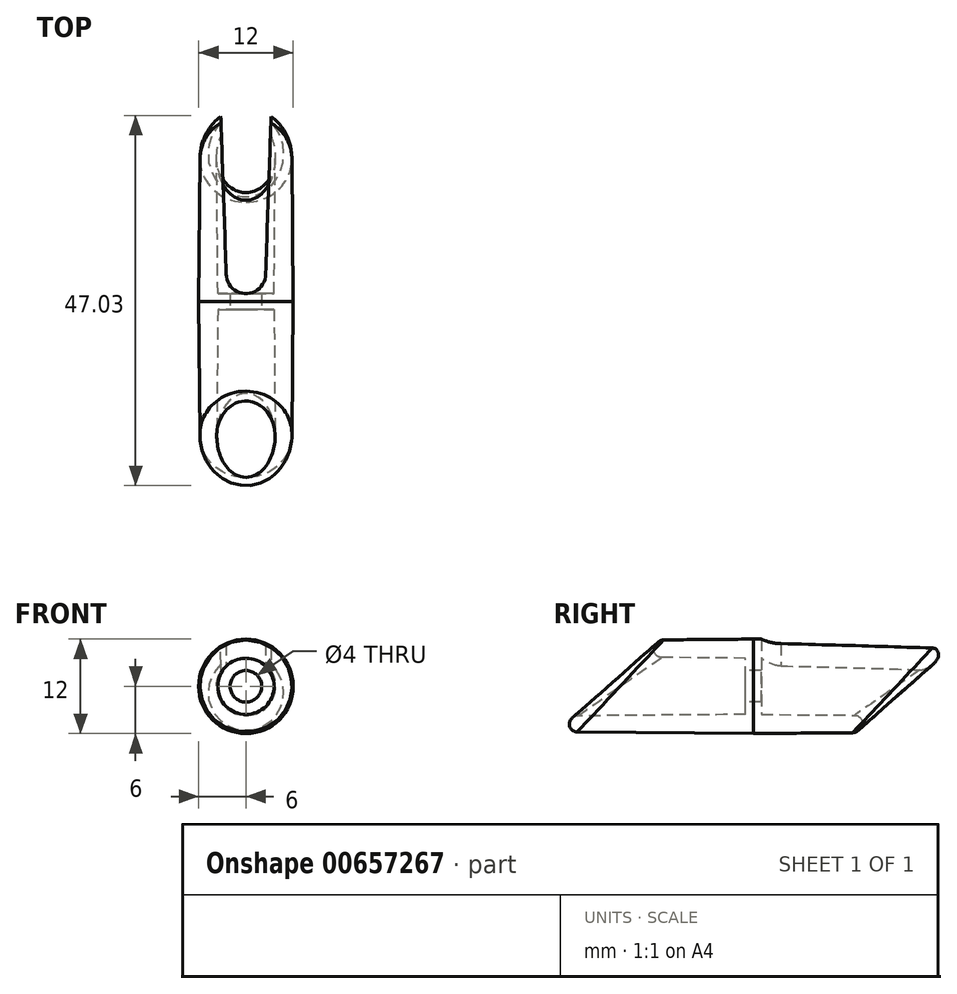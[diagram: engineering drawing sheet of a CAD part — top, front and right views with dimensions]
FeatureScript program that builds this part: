
annotation { "Feature Type Name" : "Feature", "Feature Type Description" : "" }
export const myFeature = defineFeature(function(context is Context, id is Id, definition is map)
    precondition{}
    {
        {
            var Q0;
            Q0=qCreatedBy(makeId("Right.planeOp"),FACE);
            var sketch = newSketch(context, id + "F0", { "sketchPlane" : qUnion([Q0])});
            skLineSegment(sketch, "E0", {"start": v(0, 0) * mm, "end": v(360.3, 0) * mm, "construction": true});
            skLineSegment(sketch, "E1", {"start": v(0, 0) * mm, "end": v(0, 2) * mm, "construction": true});
            skLineSegment(sketch, "E2", {"start": v(0, 2) * mm, "end": v(1, 2) * mm});
            skLineSegment(sketch, "E3", {"start": v(1, 2) * mm, "end": v(1, 3.57) * mm});
            skLineSegment(sketch, "E4", {"start": v(1, 3.57) * mm, "end": v(303.63, 3.57) * mm, "construction": true});
            skLineSegment(sketch, "E5", {"start": v(1, 3.57) * mm, "end": v(25, 3.78) * mm});
            skLineSegment(sketch, "E6", {"start": v(0, 6) * mm, "end": v(0, 106.1) * mm, "construction": true});
            skLineSegment(sketch, "E7", {"start": v(0, 6) * mm, "end": v(82.2, 6) * mm, "construction": true});
            skLineSegment(sketch, "E8", {"start": v(0, 6) * mm, "end": v(25, 5.78) * mm});
            skLineSegment(sketch, "E9", {"start": v(25, 3.78) * mm, "end": v(25, 5.78) * mm});
            skLineSegment(sketch, "E10.MirrorCS", {"start": v(0, 2) * mm, "end": v(-1, 2) * mm});
            skLineSegment(sketch, "E11.MirrorCS", {"start": v(-1, 2) * mm, "end": v(-1, 3.57) * mm});
            skLineSegment(sketch, "E12.MirrorCS", {"start": v(-1, 3.57) * mm, "end": v(-25, 3.78) * mm});
            skLineSegment(sketch, "E13.MirrorCS", {"start": v(-25, 3.78) * mm, "end": v(-25, 5.78) * mm});
            skLineSegment(sketch, "E14.MirrorCS", {"start": v(0, 6) * mm, "end": v(-25, 5.78) * mm});
            skSolve(sketch);
        }
        {
            var Q0;
            Q0=makeQuery(id+"F0.imprint","IMPRINT",FACE,{"disambiguationData":[TD([[makeQuery(id+"F0.imprint","IMPRINT",EDGE,{"derivedFrom":sQuery(id+"F0.wireOp",EDGE,"E2")}),1.0]])]});
            var Q1;
            Q1=sQuery(id+"F0.wireOp",EDGE,"E0");
            revolve(context, id + "F1", {"entities" : qUnion([Q0]), "axis" : qUnion([Q1]), "revolveType" : RevolveType.FULL});
        }
        {
            var Q0;
            Q0=qCreatedBy(makeId("Top.planeOp"),FACE);
            var sketch = newSketch(context, id + "F2", { "sketchPlane" : qUnion([Q0])});
            skLineSegment(sketch, "E15", {"start": v(2, 1) * mm, "end": v(3.57, 1) * mm, "construction": true});
            skLineSegment(sketch, "E16", {"start": v(-3.57, 1) * mm, "end": v(-2, 1) * mm, "construction": true});
            skLineSegment(sketch, "E17", {"start": v(2, 1) * mm, "end": v(-2, 1) * mm, "construction": true});
            skLineSegment(sketch, "E18", {"start": v(0, 1) * mm, "end": v(0, 704.1) * mm, "construction": true});
            skArc(sketch, "E19", {"start": v(-2.5, 3.5) * mm, "mid": v(0, 1) * mm, "end": v(2.5, 3.5) * mm});
            skLineSegment(sketch, "E20", {"start": v(0, 3.5) * mm, "end": v(2.5, 3.5) * mm, "construction": true});
            skLineSegment(sketch, "E21", {"start": v(2.5, 3.5) * mm, "end": v(3.22, 24.03) * mm});
            skLineSegment(sketch, "E22.MirrorCS", {"start": v(-2.5, 3.5) * mm, "end": v(-3.22, 24.03) * mm});
            skLineSegment(sketch, "E23.0", {"start": v(5.78, 25) * mm, "end": v(4.22, 25) * mm});
            skLineSegment(sketch, "E24.trimOffspring", {"start": v(-4.22, 25) * mm, "end": v(-5.78, 25) * mm});
            skPoint(sketch, "E25.orphan", {"position": v(-3.32, 27.03) * mm});
            skPoint(sketch, "E26.start.orphan", {"position": v(3.32, 27.03) * mm});
            skPoint(sketch, "E27.visualSharp", {"position": v(3.25, 25) * mm});
            skArc(sketch, "E27.filletArc", {"start": v(4.22, 25) * mm, "mid": v(3.52, 24.72) * mm, "end": v(3.22, 24.03) * mm});
            skPoint(sketch, "E28.visualSharp", {"position": v(-3.25, 25) * mm});
            skArc(sketch, "E28.filletArc", {"start": v(-3.22, 24.03) * mm, "mid": v(-3.52, 24.72) * mm, "end": v(-4.22, 25) * mm});
            skLineSegment(sketch, "E29", {"start": v(5.78, 25) * mm, "end": v(5.78, 27.96) * mm});
            skLineSegment(sketch, "E30", {"start": v(5.78, 27.96) * mm, "end": v(-6, 27.96) * mm});
            skLineSegment(sketch, "E31", {"start": v(-6, 27.96) * mm, "end": v(-5.78, 25) * mm});
            skSolve(sketch);
        }
        {
            var Q0;
            Q0=qSketchRegion(id+"F2",true);
            extrude(context, id + "F3", {"entities" : qUnion([Q0]), "operationType" : NewBodyOperationType.REMOVE, "depth" : 25 * mm, "offsetDistance" : 25 * mm});
        }
        {
            var Q0;
            Q0=qCreatedBy(makeId("Right.planeOp"),FACE);
            var sketch = newSketch(context, id + "F4", { "sketchPlane" : qUnion([Q0])});
            skLineSegment(sketch, "E32", {"start": v(-25, 5.78) * mm, "end": v(0, 6) * mm, "construction": true});
            skLineSegment(sketch, "E33", {"start": v(0, -6) * mm, "end": v(-25, -5.78) * mm, "construction": true});
            skLineSegment(sketch, "E34", {"start": v(27.27, 6.71) * mm, "end": v(9.74, -8.75) * mm});
            skLineSegment(sketch, "E35", {"start": v(-25, -5.78) * mm, "end": v(-3.2, 13.45) * mm});
            skLineSegment(sketch, "E36", {"start": v(-25, -5.78) * mm, "end": v(-29.65, -5.74) * mm});
            skLineSegment(sketch, "E37", {"start": v(-29.65, -5.74) * mm, "end": v(-29.65, 14.92) * mm});
            skLineSegment(sketch, "E38", {"start": v(-29.65, 14.92) * mm, "end": v(-3.2, 13.45) * mm});
            skLineSegment(sketch, "E39", {"start": v(9.74, -8.75) * mm, "end": v(32.4, -8.95) * mm});
            skLineSegment(sketch, "E40", {"start": v(32.4, -8.95) * mm, "end": v(32.4, 6.67) * mm});
            skLineSegment(sketch, "E41", {"start": v(32.4, 6.67) * mm, "end": v(27.27, 6.71) * mm});
            skSolve(sketch);
        }
        {
            var Q0;
            Q0=qSketchRegion(id+"F4",true);
            extrude(context, id + "F5", {"entities" : qUnion([Q0]), "operationType" : NewBodyOperationType.REMOVE, "oppositeDirection" : true, "depth" : 25 * mm, "offsetDistance" : 25 * mm, "symmetric" : true});
        }
        {
            var Q0;
            Q0=makeQuery(id+"F5.boolean.opBoolean","INTERSECT",EDGE,{"derivedFrom":[makeQuery(id+"F1.opRevolve","SWEPT_FACE",FACE,{"disambiguationData":[OSD([sQuery(id+"F0.wireOp",EDGE,"E8")])]}),makeQuery(id+"F5.opExtrude","SWEPT_FACE",FACE,{"disambiguationData":[OSD([sQuery(id+"F4.wireOp",EDGE,"E34")])]})]});
            var Q1;
            Q1=makeQuery(id+"F5.boolean.opBoolean","INTERSECT",EDGE,{"derivedFrom":[makeQuery(id+"F1.opRevolve","SWEPT_FACE",FACE,{"disambiguationData":[OSD([sQuery(id+"F0.wireOp",EDGE,"E5")])]}),makeQuery(id+"F5.opExtrude","SWEPT_FACE",FACE,{"disambiguationData":[OSD([sQuery(id+"F4.wireOp",EDGE,"E34")])]})]});
            var Q2;
            Q2=makeQuery(id+"F5.boolean.opBoolean","INTERSECT",EDGE,{"derivedFrom":[makeQuery(id+"F1.opRevolve","SWEPT_FACE",FACE,{"disambiguationData":[OSD([sQuery(id+"F0.wireOp",EDGE,"E14.MirrorCS")])]}),makeQuery(id+"F5.opExtrude","SWEPT_FACE",FACE,{"disambiguationData":[OSD([sQuery(id+"F4.wireOp",EDGE,"E35")])]})]});
            var Q3;
            Q3=makeQuery(id+"F5.boolean.opBoolean","INTERSECT",EDGE,{"derivedFrom":[makeQuery(id+"F1.opRevolve","SWEPT_FACE",FACE,{"disambiguationData":[OSD([sQuery(id+"F0.wireOp",EDGE,"E12.MirrorCS")])]}),makeQuery(id+"F5.opExtrude","SWEPT_FACE",FACE,{"disambiguationData":[OSD([sQuery(id+"F4.wireOp",EDGE,"E35")])]})]});
            fillet(context, id + "F6", {"entities" : qUnion([Q0, Q1, Q2, Q3]), "radius" : 1 * mm, "tangentPropagation" : true, "allowEdgeOverflow" : false});
        }
    });
